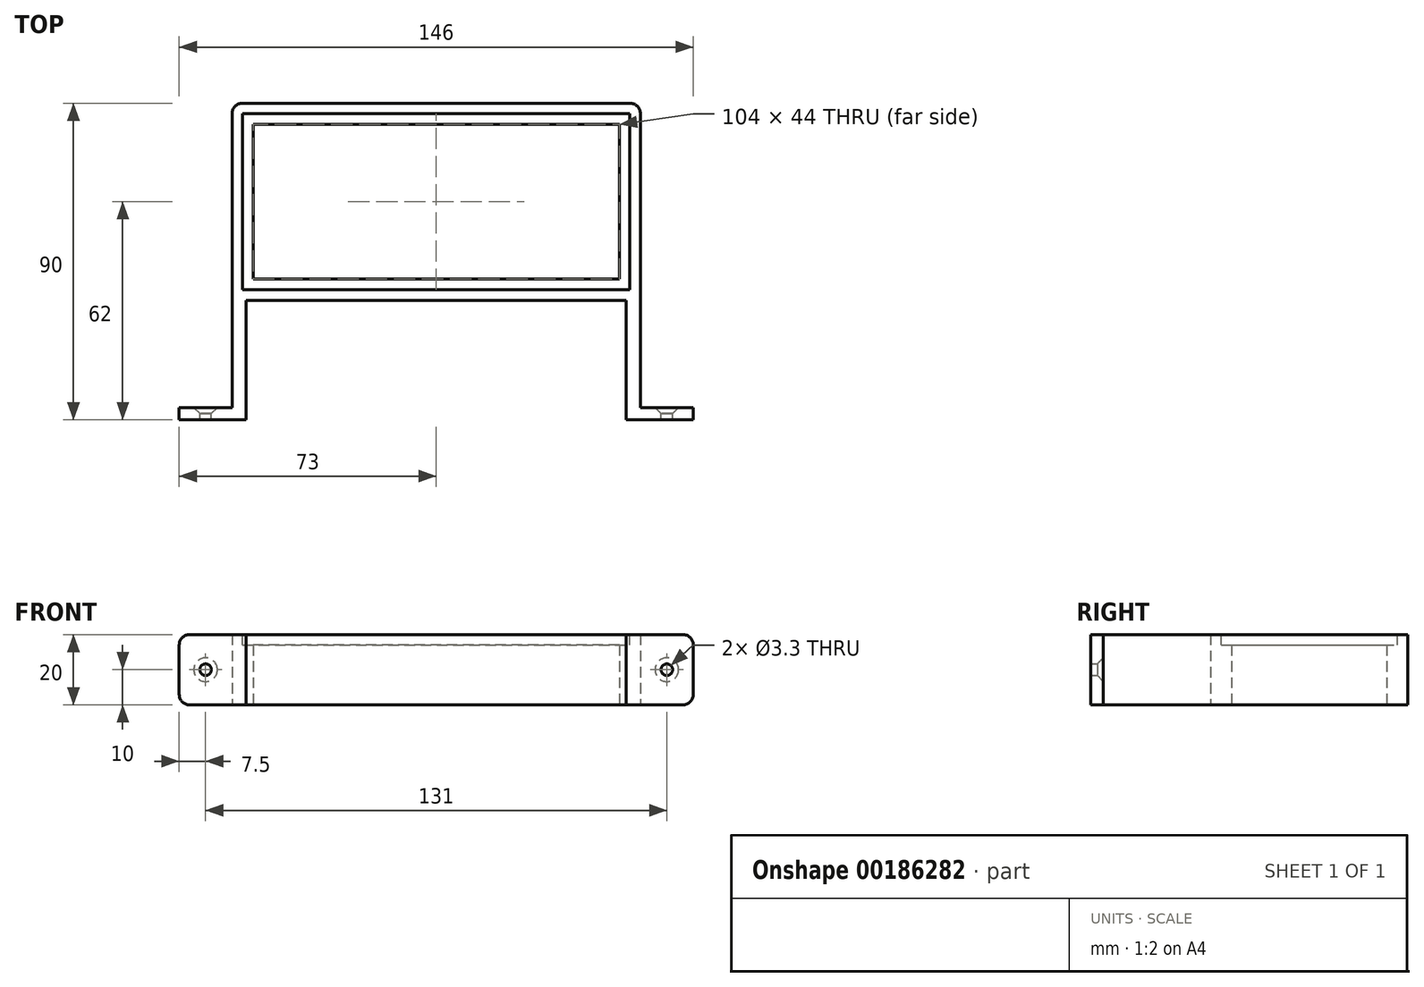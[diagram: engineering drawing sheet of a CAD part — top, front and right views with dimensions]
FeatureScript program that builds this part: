
annotation { "Feature Type Name" : "Feature", "Feature Type Description" : "" }
export const myFeature = defineFeature(function(context is Context, id is Id, definition is map)
    precondition{}
    {
        {
            var Q0;
            Q0=qCreatedBy(makeId("Top.planeOp"),FACE);
            var sketch = newSketch(context, id + "F0", { "sketchPlane" : qUnion([Q0])});
            skLineSegment(sketch, "E0.bottom", {"start": v(58, -28) * mm, "end": v(-58, -28) * mm});
            skLineSegment(sketch, "E0.top", {"start": v(58, 28) * mm, "end": v(-58, 28) * mm});
            skLineSegment(sketch, "E0.left", {"start": v(58, -28) * mm, "end": v(58, 28) * mm});
            skLineSegment(sketch, "E0.right", {"start": v(-58, -28) * mm, "end": v(-58, 28) * mm});
            skPoint(sketch, "E0.middle", {"position": v(0, 0) * mm});
            skLineSegment(sketch, "E1.bottom", {"start": v(52, -22) * mm, "end": v(-52, -22) * mm});
            skLineSegment(sketch, "E1.top", {"start": v(52, 22) * mm, "end": v(-52, 22) * mm});
            skLineSegment(sketch, "E1.left", {"start": v(52, -22) * mm, "end": v(52, 22) * mm});
            skLineSegment(sketch, "E1.right", {"start": v(-52, -22) * mm, "end": v(-52, 22) * mm});
            skSolve(sketch);
        }
        {
            var Q0;
            Q0=makeQuery(id+"F0.imprint","IMPRINT",FACE,{"disambiguationData":[TD([[makeQuery(id+"F0.imprint","IMPRINT",EDGE,{"derivedFrom":sQuery(id+"F0.wireOp",EDGE,"E0.bottom")}),-1.0]])]});
            extrude(context, id + "F1", {"entities" : qUnion([Q0]), "depth" : 20 * mm, "offsetDistance" : 25 * mm});
        }
        {
            var Q0;
            Q0=makeQuery(id+"F1.opExtrude","CAP_FACE",FACE,{"disambiguationData":[OSD([sQuery(id+"F0.wireOp",EDGE,"E0.bottom"),sQuery(id+"F0.wireOp",EDGE,"E0.top"),sQuery(id+"F0.wireOp",EDGE,"E0.left"),sQuery(id+"F0.wireOp",EDGE,"E0.right"),sQuery(id+"F0.wireOp",EDGE,"E1.bottom"),sQuery(id+"F0.wireOp",EDGE,"E1.top"),sQuery(id+"F0.wireOp",EDGE,"E1.left"),sQuery(id+"F0.wireOp",EDGE,"E1.right")])],"isStart":false});
            var sketch = newSketch(context, id + "F2", { "sketchPlane" : qUnion([Q0])});
            skLineSegment(sketch, "E2.bottom", {"start": v(-55, -25) * mm, "end": v(55, -25) * mm});
            skLineSegment(sketch, "E2.top", {"start": v(-55, 25) * mm, "end": v(55, 25) * mm});
            skLineSegment(sketch, "E2.left", {"start": v(-55, -25) * mm, "end": v(-55, 25) * mm});
            skLineSegment(sketch, "E2.right", {"start": v(55, -25) * mm, "end": v(55, 25) * mm});
            skPoint(sketch, "E2.middle", {"position": v(0, 0) * mm});
            skSolve(sketch);
        }
        {
            var Q0;
            Q0=makeQuery(id+"F2.imprint","IMPRINT",FACE,{"disambiguationData":[TD([[makeQuery(id+"F2.imprint","IMPRINT",EDGE,{"derivedFrom":sQuery(id+"F2.wireOp",EDGE,"E2.bottom")}),1.0]])]});
            extrude(context, id + "F3", {"entities" : qUnion([Q0]), "operationType" : NewBodyOperationType.REMOVE, "oppositeDirection" : true, "depth" : 3 * mm, "offsetDistance" : 25 * mm});
        }
        {
            var Q0;
            Q0=makeQuery(id+"F1.opExtrude","SWEPT_FACE",FACE,{"disambiguationData":[OSD([sQuery(id+"F0.wireOp",EDGE,"E0.bottom")])]});
            var sketch = newSketch(context, id + "F4", { "sketchPlane" : qUnion([Q0])});
            skLineSegment(sketch, "E3.bottom", {"start": v(-58, 20) * mm, "end": v(-54, 20) * mm});
            skLineSegment(sketch, "E3.top", {"start": v(-58, 0) * mm, "end": v(-54, 0) * mm});
            skLineSegment(sketch, "E3.left", {"start": v(-58, 20) * mm, "end": v(-58, 0) * mm});
            skLineSegment(sketch, "E3.right", {"start": v(-54, 20) * mm, "end": v(-54, 0) * mm});
            skLineSegment(sketch, "E4.bottom", {"start": v(58, 20) * mm, "end": v(54, 20) * mm});
            skLineSegment(sketch, "E4.top", {"start": v(58, 0) * mm, "end": v(54, 0) * mm});
            skLineSegment(sketch, "E4.left", {"start": v(58, 20) * mm, "end": v(58, 0) * mm});
            skLineSegment(sketch, "E4.right", {"start": v(54, 20) * mm, "end": v(54, 0) * mm});
            skSolve(sketch);
        }
        {
            var Q0;
            Q0=makeQuery(id+"F4.imprint","IMPRINT",FACE,{"disambiguationData":[TD([[makeQuery(id+"F4.imprint","IMPRINT",EDGE,{"derivedFrom":sQuery(id+"F4.wireOp",EDGE,"E3.bottom")}),1.0]])]});
            var Q1;
            Q1=makeQuery(id+"F4.imprint","IMPRINT",FACE,{"disambiguationData":[TD([[makeQuery(id+"F4.imprint","IMPRINT",EDGE,{"derivedFrom":sQuery(id+"F4.wireOp",EDGE,"E4.bottom")}),1.0]])]});
            extrude(context, id + "F5", {"entities" : qUnion([Q0, Q1]), "operationType" : NewBodyOperationType.ADD, "depth" : 34 * mm, "offsetDistance" : 25 * mm});
        }
        {
            var Q0;
            Q0=makeQuery(id+"F5.boolean.opBoolean","MERGE",FACE,{"derivedFrom":[makeQuery(id+"F1.opExtrude","SWEPT_FACE",FACE,{"disambiguationData":[OSD([sQuery(id+"F0.wireOp",EDGE,"E0.left")])]}),makeQuery(id+"F5.opExtrude","SWEPT_FACE",FACE,{"disambiguationData":[OSD([sQuery(id+"F4.wireOp",EDGE,"E4.left")])]})]});
            var sketch = newSketch(context, id + "F6", { "sketchPlane" : qUnion([Q0])});
            skLineSegment(sketch, "E5.bottom", {"start": v(-62, 20) * mm, "end": v(-58.5, 20) * mm});
            skLineSegment(sketch, "E5.top", {"start": v(-62, 0) * mm, "end": v(-58.5, 0) * mm});
            skLineSegment(sketch, "E5.left", {"start": v(-62, 20) * mm, "end": v(-62, 0) * mm});
            skLineSegment(sketch, "E5.right", {"start": v(-58.5, 20) * mm, "end": v(-58.5, 0) * mm});
            skSolve(sketch);
        }
        {
            var Q0;
            Q0=makeQuery(id+"F6.imprint","IMPRINT",FACE,{"disambiguationData":[TD([[makeQuery(id+"F6.imprint","IMPRINT",EDGE,{"derivedFrom":sQuery(id+"F6.wireOp",EDGE,"E5.bottom")}),-1.0]])]});
            extrude(context, id + "F7", {"entities" : qUnion([Q0]), "operationType" : NewBodyOperationType.ADD, "depth" : 15 * mm, "offsetDistance" : 25 * mm});
        }
        {
            var Q0;
            Q0=makeQuery(id+"F5.boolean.opBoolean","MERGE",FACE,{"derivedFrom":[makeQuery(id+"F1.opExtrude","SWEPT_FACE",FACE,{"disambiguationData":[OSD([sQuery(id+"F0.wireOp",EDGE,"E0.right")])]}),makeQuery(id+"F5.opExtrude","SWEPT_FACE",FACE,{"disambiguationData":[OSD([sQuery(id+"F4.wireOp",EDGE,"E3.left")])]})]});
            var sketch = newSketch(context, id + "F8", { "sketchPlane" : qUnion([Q0])});
            skLineSegment(sketch, "E6.bottom", {"start": v(62, 20) * mm, "end": v(58.5, 20) * mm});
            skLineSegment(sketch, "E6.top", {"start": v(62, 0) * mm, "end": v(58.5, 0) * mm});
            skLineSegment(sketch, "E6.left", {"start": v(62, 20) * mm, "end": v(62, 0) * mm});
            skLineSegment(sketch, "E6.right", {"start": v(58.5, 20) * mm, "end": v(58.5, 0) * mm});
            skSolve(sketch);
        }
        {
            var Q0;
            Q0=makeQuery(id+"F8.imprint","IMPRINT",FACE,{"disambiguationData":[TD([[makeQuery(id+"F8.imprint","IMPRINT",EDGE,{"derivedFrom":sQuery(id+"F8.wireOp",EDGE,"E6.bottom")}),1.0]])]});
            extrude(context, id + "F9", {"entities" : qUnion([Q0]), "operationType" : NewBodyOperationType.ADD, "depth" : 15 * mm, "offsetDistance" : 25 * mm});
        }
        {
            var Q0;
            Q0=makeQuery(id+"F7.opExtrude","SWEPT_FACE",FACE,{"disambiguationData":[OSD([sQuery(id+"F6.wireOp",EDGE,"E5.right")])]});
            var sketch = newSketch(context, id + "F10", { "sketchPlane" : qUnion([Q0])});
            skPoint(sketch, "E7", {"position": v(-65.5, 10) * mm});
            skPoint(sketch, "E7.positionSnap0", {"position": v(-65.5, 20) * mm});
            skPoint(sketch, "E7.positionSnap1", {"position": v(-73, 10) * mm});
            skPoint(sketch, "E8", {"position": v(-65.5, 0) * mm});
            skSolve(sketch);
        }
        {
            var Q0;
            Q0=sQuery(id+"F10.wireOp",VERTEX,"E7");
            var Q1;
            Q1=makeQuery(id+"F1.opExtrude","SWEPT_BODY",BODY,{"disambiguationData":[OSD([sQuery(id+"F0.wireOp",EDGE,"E0.bottom"),sQuery(id+"F0.wireOp",EDGE,"E0.top"),sQuery(id+"F0.wireOp",EDGE,"E0.left"),sQuery(id+"F0.wireOp",EDGE,"E0.right"),sQuery(id+"F0.wireOp",EDGE,"E1.bottom"),sQuery(id+"F0.wireOp",EDGE,"E1.top"),sQuery(id+"F0.wireOp",EDGE,"E1.left"),sQuery(id+"F0.wireOp",EDGE,"E1.right")])]});
            hole(context, id + "F11", {"style" : HoleStyle.C_SINK, "endStyle" : HoleEndStyle.BLIND, "standardTappedOrClearance" : lookupTablePath({ "standard" : "ISO", "fit" : "Normal", "size" : "M3", "type" : "Clearance" }), "standardBlindInLast" : lookupTablePath({ "fit" : "Standard", "standard" : "ISO", "size" : "M3", "type" : "Clearance" }), "holeDiameter" : 3.3 * mm, "cSinkDiameter" : 6.72 * mm, "cSinkAngle" : 90 * degree, "majorDiameter" : 5 * mm, "holeDepth" : 5 * mm, "isTappedThrough" : true, "tappedDepth" : 12 * mm, "tapClearance" : 3, "startFromSketch" : true, "locations" : qUnion([Q0]), "scope" : qUnion([Q1])});
        }
        {
            var Q0;
            Q0=makeQuery(id+"F9.opExtrude","SWEPT_FACE",FACE,{"disambiguationData":[OSD([sQuery(id+"F8.wireOp",EDGE,"E6.right")])]});
            var sketch = newSketch(context, id + "F12", { "sketchPlane" : qUnion([Q0])});
            skPoint(sketch, "E9", {"position": v(65.5, 10) * mm});
            skPoint(sketch, "E9.positionSnap1", {"position": v(58, 10) * mm});
            skPoint(sketch, "E10", {"position": v(65.5, 20) * mm});
            skPoint(sketch, "E11", {"position": v(65.5, 0) * mm});
            skSolve(sketch);
        }
        {
            var Q0;
            Q0=sQuery(id+"F12.wireOp",VERTEX,"E9");
            var Q1;
            Q1=makeQuery(id+"F1.opExtrude","SWEPT_BODY",BODY,{"disambiguationData":[OSD([sQuery(id+"F0.wireOp",EDGE,"E0.bottom"),sQuery(id+"F0.wireOp",EDGE,"E0.top"),sQuery(id+"F0.wireOp",EDGE,"E0.left"),sQuery(id+"F0.wireOp",EDGE,"E0.right"),sQuery(id+"F0.wireOp",EDGE,"E1.bottom"),sQuery(id+"F0.wireOp",EDGE,"E1.top"),sQuery(id+"F0.wireOp",EDGE,"E1.left"),sQuery(id+"F0.wireOp",EDGE,"E1.right")])]});
            hole(context, id + "F13", {"style" : HoleStyle.C_SINK, "endStyle" : HoleEndStyle.BLIND, "standardTappedOrClearance" : lookupTablePath({ "standard" : "ISO", "fit" : "Normal", "size" : "M3", "type" : "Clearance" }), "standardBlindInLast" : lookupTablePath({ "fit" : "Standard", "standard" : "ISO", "size" : "M3", "type" : "Clearance" }), "holeDiameter" : 3.3 * mm, "cSinkDiameter" : 6.72 * mm, "cSinkAngle" : 90 * degree, "majorDiameter" : 5 * mm, "holeDepth" : 5 * mm, "isTappedThrough" : true, "tappedDepth" : 12 * mm, "tapClearance" : 3, "startFromSketch" : true, "locations" : qUnion([Q0]), "scope" : qUnion([Q1])});
        }
        {
            var Q0;
            Q0=makeQuery(id+"F1.opExtrude","SWEPT_EDGE",EDGE,{"disambiguationData":[OSD([sQuery(id+"F0.wireOp",EDGE,"E0.top"),sQuery(id+"F0.wireOp",EDGE,"E0.left")])]});
            var Q1;
            Q1=makeQuery(id+"F1.opExtrude","SWEPT_EDGE",EDGE,{"disambiguationData":[OSD([sQuery(id+"F0.wireOp",EDGE,"E0.top"),sQuery(id+"F0.wireOp",EDGE,"E0.right")])]});
            var Q2;
            Q2=makeQuery(id+"F7.opExtrude","CAP_EDGE",EDGE,{"disambiguationData":[OSD([sQuery(id+"F6.wireOp",EDGE,"E5.top")])],"isStart":false});
            var Q3;
            Q3=makeQuery(id+"F7.opExtrude","CAP_EDGE",EDGE,{"disambiguationData":[OSD([sQuery(id+"F6.wireOp",EDGE,"E5.bottom")])],"isStart":false});
            var Q4;
            Q4=makeQuery(id+"F9.opExtrude","CAP_EDGE",EDGE,{"disambiguationData":[OSD([sQuery(id+"F8.wireOp",EDGE,"E6.bottom")])],"isStart":false});
            var Q5;
            Q5=makeQuery(id+"F9.opExtrude","CAP_EDGE",EDGE,{"disambiguationData":[OSD([sQuery(id+"F8.wireOp",EDGE,"E6.top")])],"isStart":false});
            fillet(context, id + "F14", {"entities" : qUnion([Q0, Q1, Q2, Q3, Q4, Q5]), "radius" : 3 * mm, "tangentPropagation" : true, "allowEdgeOverflow" : false});
        }
    });
